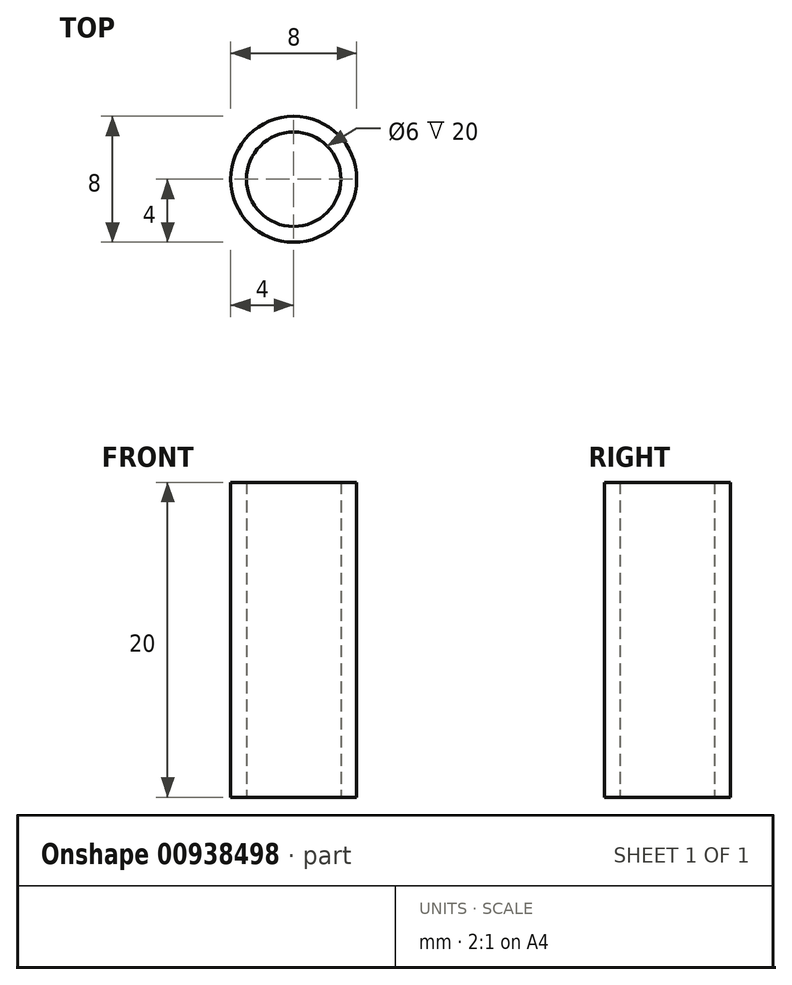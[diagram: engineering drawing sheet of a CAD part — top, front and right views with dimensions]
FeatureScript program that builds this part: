
annotation { "Feature Type Name" : "Feature", "Feature Type Description" : "" }
export const myFeature = defineFeature(function(context is Context, id is Id, definition is map)
    precondition{}
    {
        {
            var Q0;
            Q0=qCreatedBy(makeId("Top.planeOp"),FACE);
            var sketch = newSketch(context, id + "F0", { "sketchPlane" : qUnion([Q0])});
            skCircle(sketch, "E0", {"center": v(0, 0) * mm, "radius": 4 * mm});
            skCircle(sketch, "E1", {"center": v(0, 0) * mm, "radius": 3 * mm});
            skSolve(sketch);
        }
        {
            var Q0;
            Q0 = qSketchRegion(id + "F0", true);
            extrude(context, id + "F1", {"entities" : qUnion([Q0]), "depth" : 20 * mm, "offsetDistance" : 25 * mm});
        }
    });
